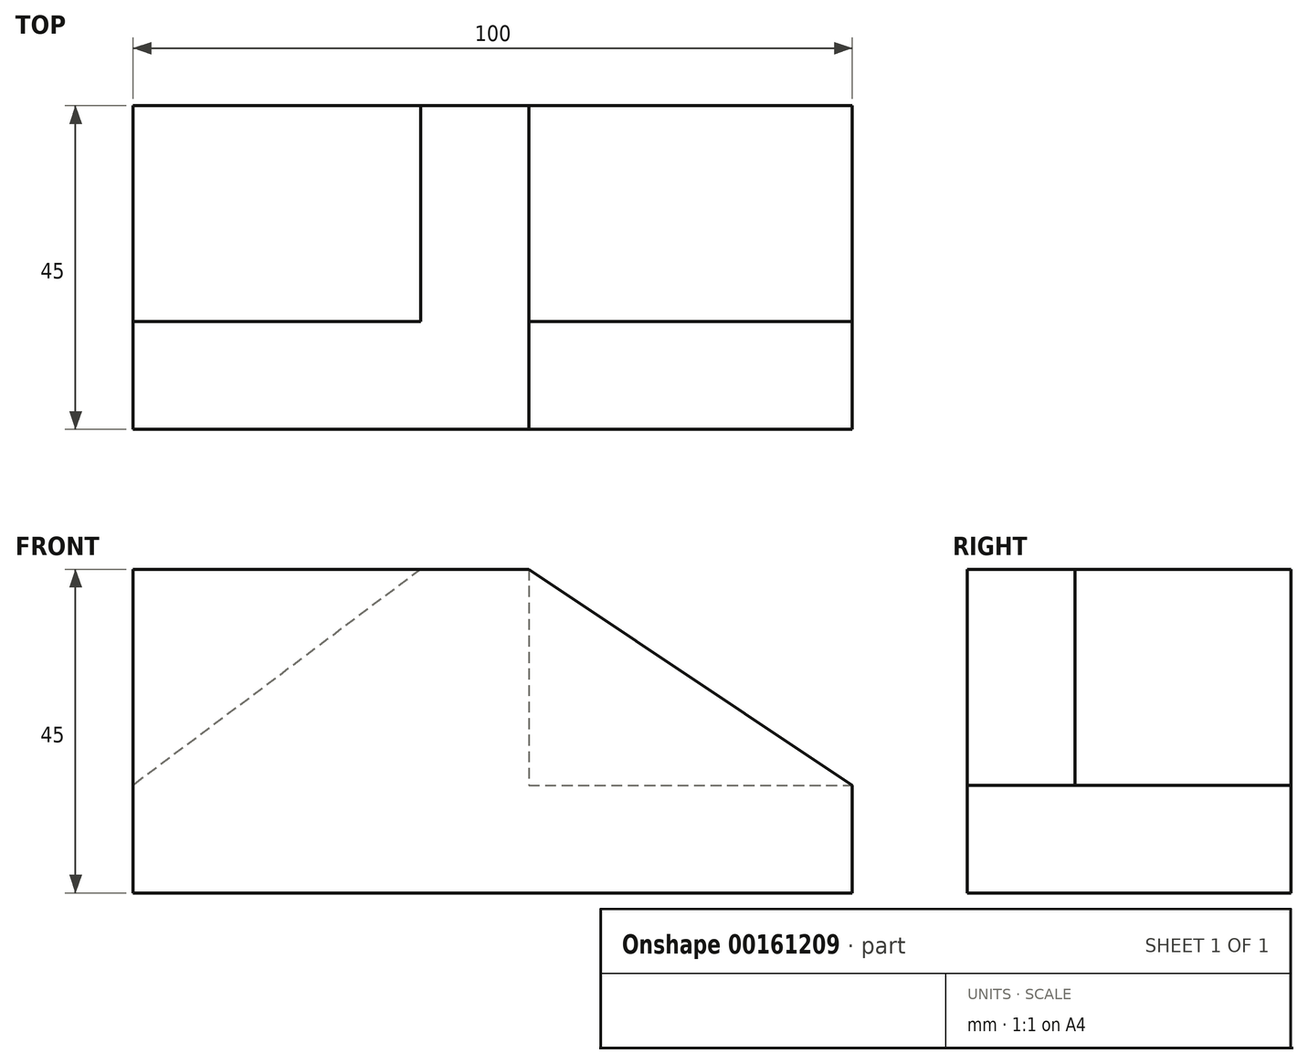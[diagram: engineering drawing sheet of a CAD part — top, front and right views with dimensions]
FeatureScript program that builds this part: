
annotation { "Feature Type Name" : "Feature", "Feature Type Description" : "" }
export const myFeature = defineFeature(function(context is Context, id is Id, definition is map)
    precondition{}
    {
        {
            var Q0;
            Q0=qCreatedBy(makeId("Top.planeOp"),FACE);
            var sketch = newSketch(context, id + "F0", { "sketchPlane" : qUnion([Q0])});
            skLineSegment(sketch, "E0.bottom", {"start": v(-52.3, 9.41) * mm, "end": v(47.7, 9.41) * mm});
            skLineSegment(sketch, "E0.top", {"start": v(-52.3, -35.59) * mm, "end": v(47.7, -35.59) * mm});
            skLineSegment(sketch, "E0.left", {"start": v(-52.3, 9.41) * mm, "end": v(-52.3, -35.59) * mm});
            skLineSegment(sketch, "E0.right", {"start": v(47.7, 9.41) * mm, "end": v(47.7, -35.59) * mm});
            skSolve(sketch);
        }
        {
            var Q0;
            Q0 = qSketchRegion(id + "F0", true);
            extrude(context, id + "F1", {"entities" : qUnion([Q0]), "depth" : 15 * mm});
        }
        {
            var Q0;
            Q0=makeQuery(id+"F1.opExtrude","CAP_FACE",FACE,{"disambiguationData":[OSD([sQuery(id+"F0.wireOp",EDGE,"E0.bottom"),sQuery(id+"F0.wireOp",EDGE,"E0.top"),sQuery(id+"F0.wireOp",EDGE,"E0.left"),sQuery(id+"F0.wireOp",EDGE,"E0.right")])],"isStart":false});
            var sketch = newSketch(context, id + "F2", { "sketchPlane" : qUnion([Q0])});
            skLineSegment(sketch, "E1", {"start": v(47.7, 9.41) * mm, "end": v(2.7, 9.41) * mm});
            skLineSegment(sketch, "E2", {"start": v(2.7, 9.41) * mm, "end": v(-12.3, 9.41) * mm});
            skLineSegment(sketch, "E3", {"start": v(2.7, 9.41) * mm, "end": v(2.7, -35.59) * mm});
            skLineSegment(sketch, "E4", {"start": v(2.7, -35.59) * mm, "end": v(-12.3, -35.59) * mm});
            skLineSegment(sketch, "E5", {"start": v(-12.3, -35.59) * mm, "end": v(-52.3, -35.59) * mm});
            skLineSegment(sketch, "E6", {"start": v(-52.3, -35.59) * mm, "end": v(-52.3, -20.59) * mm});
            skLineSegment(sketch, "E7", {"start": v(-52.3, -20.59) * mm, "end": v(-12.3, -20.59) * mm});
            skLineSegment(sketch, "E8", {"start": v(-12.3, -20.59) * mm, "end": v(-12.3, 9.41) * mm});
            skSolve(sketch);
        }
        {
            var Q0;
            Q0 = qSketchRegion(id + "F2", true);
            extrude(context, id + "F3", {"entities" : qUnion([Q0]), "operationType" : NewBodyOperationType.ADD, "depth" : 30 * mm});
        }
        {
            var Q0;
            Q0=makeQuery(id+"F3.boolean.opBoolean","MERGE",FACE,{"derivedFrom":[makeQuery(id+"F1.opExtrude","SWEPT_FACE",FACE,{"disambiguationData":[OSD([sQuery(id+"F0.wireOp",EDGE,"E0.bottom")])]}),makeQuery(id+"F3.opExtrude","SWEPT_FACE",FACE,{"disambiguationData":[OSD([sQuery(id+"F2.wireOp",EDGE,"E2")])]})]});
            var sketch = newSketch(context, id + "F4", { "sketchPlane" : qUnion([Q0])});
            skLineSegment(sketch, "E9", {"start": v(12.3, 45) * mm, "end": v(52.3, 15) * mm});
            skLineSegment(sketch, "E10", {"start": v(52.3, 15) * mm, "end": v(12.3, 15) * mm});
            skLineSegment(sketch, "E11", {"start": v(12.3, 15) * mm, "end": v(12.3, 45) * mm});
            skSolve(sketch);
        }
        {
            var Q0;
            Q0 = qSketchRegion(id + "F4", true);
            extrude(context, id + "F5", {"entities" : qUnion([Q0]), "operationType" : NewBodyOperationType.ADD, "oppositeDirection" : true, "depth" : 33 * mm});
        }
        {
            var Q0;
            Q0=makeQuery(id+"F3.boolean.opBoolean","MERGE",FACE,{"derivedFrom":[makeQuery(id+"F1.opExtrude","SWEPT_FACE",FACE,{"disambiguationData":[OSD([sQuery(id+"F0.wireOp",EDGE,"E0.top")])]}),makeQuery(id+"F3.opExtrude","SWEPT_FACE",FACE,{"disambiguationData":[OSD([sQuery(id+"F2.wireOp",EDGE,"E4"),sQuery(id+"F2.wireOp",EDGE,"E5")])]})]});
            var sketch = newSketch(context, id + "F6", { "sketchPlane" : qUnion([Q0])});
            skLineSegment(sketch, "E12", {"start": v(2.7, 45) * mm, "end": v(47.7, 15) * mm});
            skLineSegment(sketch, "E13", {"start": v(47.7, 15) * mm, "end": v(2.7, 15) * mm});
            skLineSegment(sketch, "E14", {"start": v(2.7, 15) * mm, "end": v(2.7, 45) * mm});
            skSolve(sketch);
        }
        {
            var Q0;
            Q0 = qSketchRegion(id + "F6", true);
            extrude(context, id + "F7", {"entities" : qUnion([Q0]), "operationType" : NewBodyOperationType.ADD, "oppositeDirection" : true, "depth" : 15 * mm});
        }
    });
